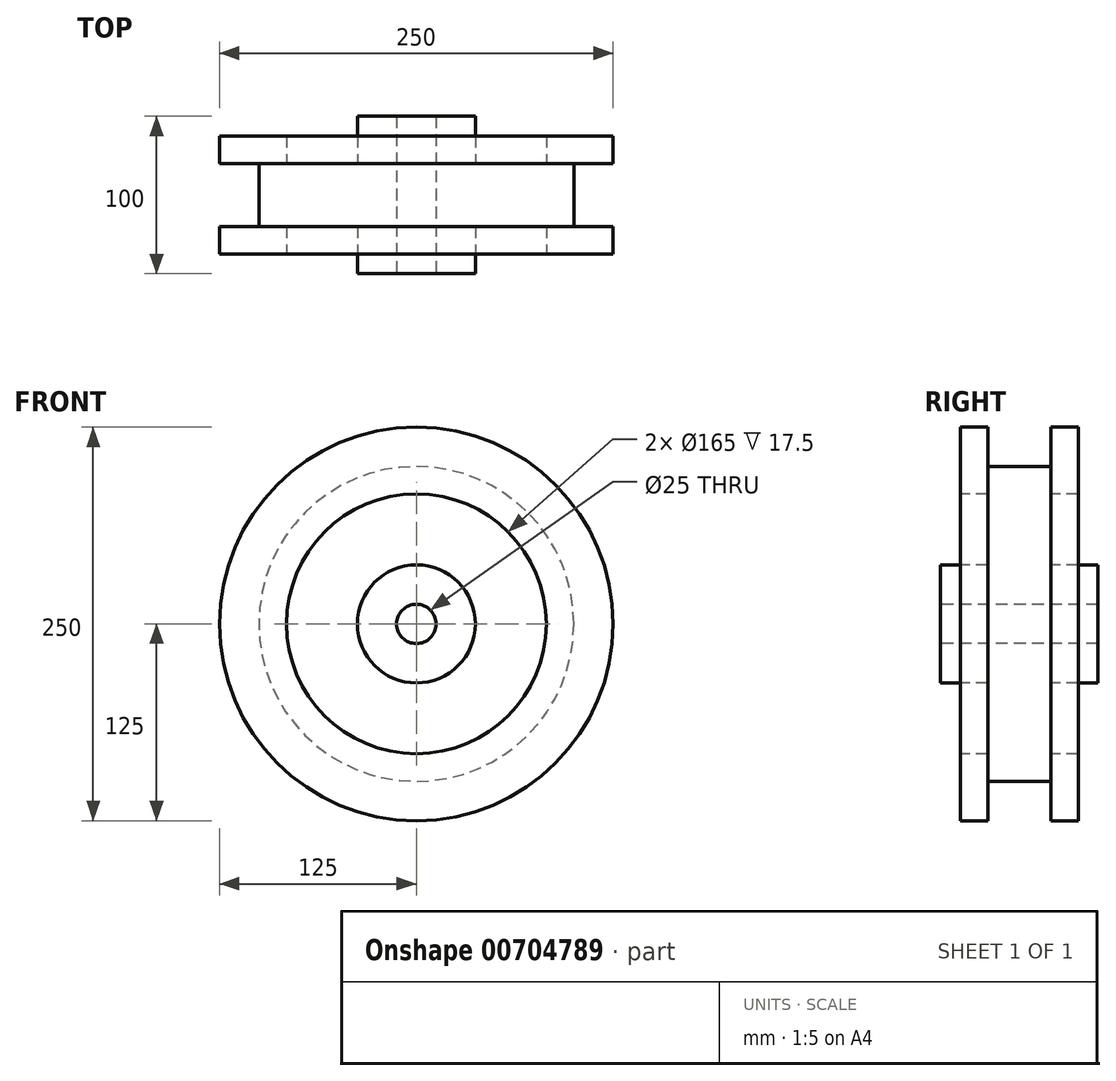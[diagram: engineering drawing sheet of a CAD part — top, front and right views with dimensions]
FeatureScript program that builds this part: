
annotation { "Feature Type Name" : "Feature", "Feature Type Description" : "" }
export const myFeature = defineFeature(function(context is Context, id is Id, definition is map)
    precondition{}
    {
        {
            var Q0;
            Q0=qCreatedBy(makeId("Right.planeOp"),FACE);
            var sketch = newSketch(context, id + "F0", { "sketchPlane" : qUnion([Q0])});
            skLineSegment(sketch, "E0", {"start": v(-66.1, 0) * mm, "end": v(66.1, 0) * mm, "construction": true});
            skLineSegment(sketch, "E1", {"start": v(0, 0) * mm, "end": v(0, 121.98) * mm, "construction": true});
            skLineSegment(sketch, "E2", {"start": v(0, 100) * mm, "end": v(-20, 100) * mm});
            skLineSegment(sketch, "E3", {"start": v(-20, 100) * mm, "end": v(-20, 125) * mm});
            skLineSegment(sketch, "E4", {"start": v(-20, 125) * mm, "end": v(-37.5, 125) * mm});
            skLineSegment(sketch, "E5", {"start": v(-37.5, 125) * mm, "end": v(-37.5, 82.5) * mm});
            skLineSegment(sketch, "E6", {"start": v(-37.5, 82.5) * mm, "end": v(-20, 82.5) * mm});
            skLineSegment(sketch, "E7", {"start": v(-20, 82.5) * mm, "end": v(-20, 37.5) * mm});
            skLineSegment(sketch, "E8", {"start": v(-20, 37.5) * mm, "end": v(-50, 37.5) * mm});
            skLineSegment(sketch, "E9", {"start": v(-50, 37.5) * mm, "end": v(-50, 12.5) * mm});
            skLineSegment(sketch, "E10", {"start": v(-50, 12.5) * mm, "end": v(0, 12.5) * mm});
            skLineSegment(sketch, "E11.MirrorCS", {"start": v(0, 100) * mm, "end": v(20, 100) * mm});
            skLineSegment(sketch, "E12.MirrorCS", {"start": v(20, 100) * mm, "end": v(20, 125) * mm});
            skLineSegment(sketch, "E13.MirrorCS", {"start": v(20, 125) * mm, "end": v(37.5, 125) * mm});
            skLineSegment(sketch, "E14.MirrorCS", {"start": v(37.5, 125) * mm, "end": v(37.5, 82.5) * mm});
            skLineSegment(sketch, "E15.MirrorCS", {"start": v(37.5, 82.5) * mm, "end": v(20, 82.5) * mm});
            skLineSegment(sketch, "E16.MirrorCS", {"start": v(20, 82.5) * mm, "end": v(20, 37.5) * mm});
            skLineSegment(sketch, "E17.MirrorCS", {"start": v(20, 37.5) * mm, "end": v(50, 37.5) * mm});
            skLineSegment(sketch, "E18.MirrorCS", {"start": v(50, 37.5) * mm, "end": v(50, 12.5) * mm});
            skLineSegment(sketch, "E19.MirrorCS", {"start": v(50, 12.5) * mm, "end": v(0, 12.5) * mm});
            skSolve(sketch);
        }
        {
            var Q0;
            Q0=makeQuery(id+"F0.imprint","IMPRINT",FACE,{"disambiguationData":[TD([[makeQuery(id+"F0.imprint","IMPRINT",EDGE,{"derivedFrom":sQuery(id+"F0.wireOp",EDGE,"E2")}),1.0]])]});
            var Q1;
            Q1=sQuery(id+"F0.wireOp",EDGE,"E0");
            revolve(context, id + "F1", {"entities" : qUnion([Q0]), "axis" : qUnion([Q1]), "revolveType" : RevolveType.FULL});
        }
    });
